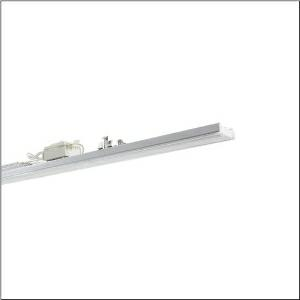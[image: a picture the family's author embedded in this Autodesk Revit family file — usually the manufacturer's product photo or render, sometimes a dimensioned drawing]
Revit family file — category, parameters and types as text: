
# Revit family: licross_r__11_recessed_ho_51tl1emn4d5s_fbf9
name_source: partatom
category: Lighting Fixtures
units: mm (PartAtom-declared; Revit-internal decimal feet)

## family parameters
Cut with Voids When Loaded = No
Host = Face
Light Source = No
Part Type = Normal
Room Calculation Point = No
Round Connector Dimension = Use Diameter
Shared = No

## types (1)
- --- (1 x LED, 13740 lm, 74.5 W, 4000K)
    Apparent Load = 75 VA
    CIE Flux Codes = 85 95 99 100 100
    Color Rendering = 80
    Color Temperature = 4000K
    Default Elevation = 1800 mm
    Description = Licross® 11 Recessed HO, luminaire insert, of sheet steel, coil coated, white, length: 1.500mm, width: 66mm, height: 67mm, LED rated luminous flux: 13.740lm, light colour: 840, control gear: ON/OFF Multilumen, with plug, 3-pole, with phase selection, mains connection: 220..240V, AC, 50/60Hz, rated input power: 75W, internal wiring halogen-free, primary light control with lens, of plastic, primary optical cover: cover, of PMMA, light emission: direct distribution, primary light characteristic: symmetric, protection rating (complete): IP40, insulation class (complete): insulation class I (protective earthing), certification: CE, ENEC, VDE, UKCA, protection symbol: D if used in an environment without relevant dust loads with corresponding accessories, impact resistance: IK06, permissible ambient temperature for indoor applications: -35..+35°C, corresponds to IFS (International Featured Standards) requirements for safety and quality in the food industry, reducing of maximum allowable ambient temperature of 5°C with ceiling mounting, packaging unit: 1 piece
    Height = 58 mm
    Lamp = 1 x LED
    Lamp Light Flux = 13740 lm
    Lamp Power = 74.5 W
    Lamp count = 1
    Length = 1500 mm
    Luminous efficacy = 184 lm/W
    Manufacturer = Siteco
    ModVariant = No
    Model = 51TL1EMN4D5S
    Mounting Place = Ceiling
    Mounting Type = Pendant
    Number of Poles = 1
    OnlyDefault = Yes
    Power Factor = 1
    Product Name = Licross® 11 Recessed HO
    Product group = luminaire insert | ceiling pendant
    ProductGroupID = 902
    Protection Class = Protection class I
    Protection Degree = IP 40
    RLX_Detail_Level = 1
    RLX_Emergency_Light_Flux = 0 lm
    RLX_Emergency_Type = 0
    RLX_Emergency_Type_DB = No
    RlxData = <blob elided: 22349 chars, md5=1af05702>
    Socket = socket
    Standby Power = 0 W
    System Light Flux = 13740 lm
    System Power = 75 W
    Type Comments = factory setting: luminous flux: 100 % | (A | C | E) | 174 mA
    Type Image = l_1296930.jpg
    URL = http://relux.com
    VarID = @adj_105825
    Voltage = 0 V
    Weight = 0.00 kg
    Width = 66 mm

## geometry (parser evidence)
native form markers: Blend x4, Sweep x11
no freeform markers — native parametric forms only
